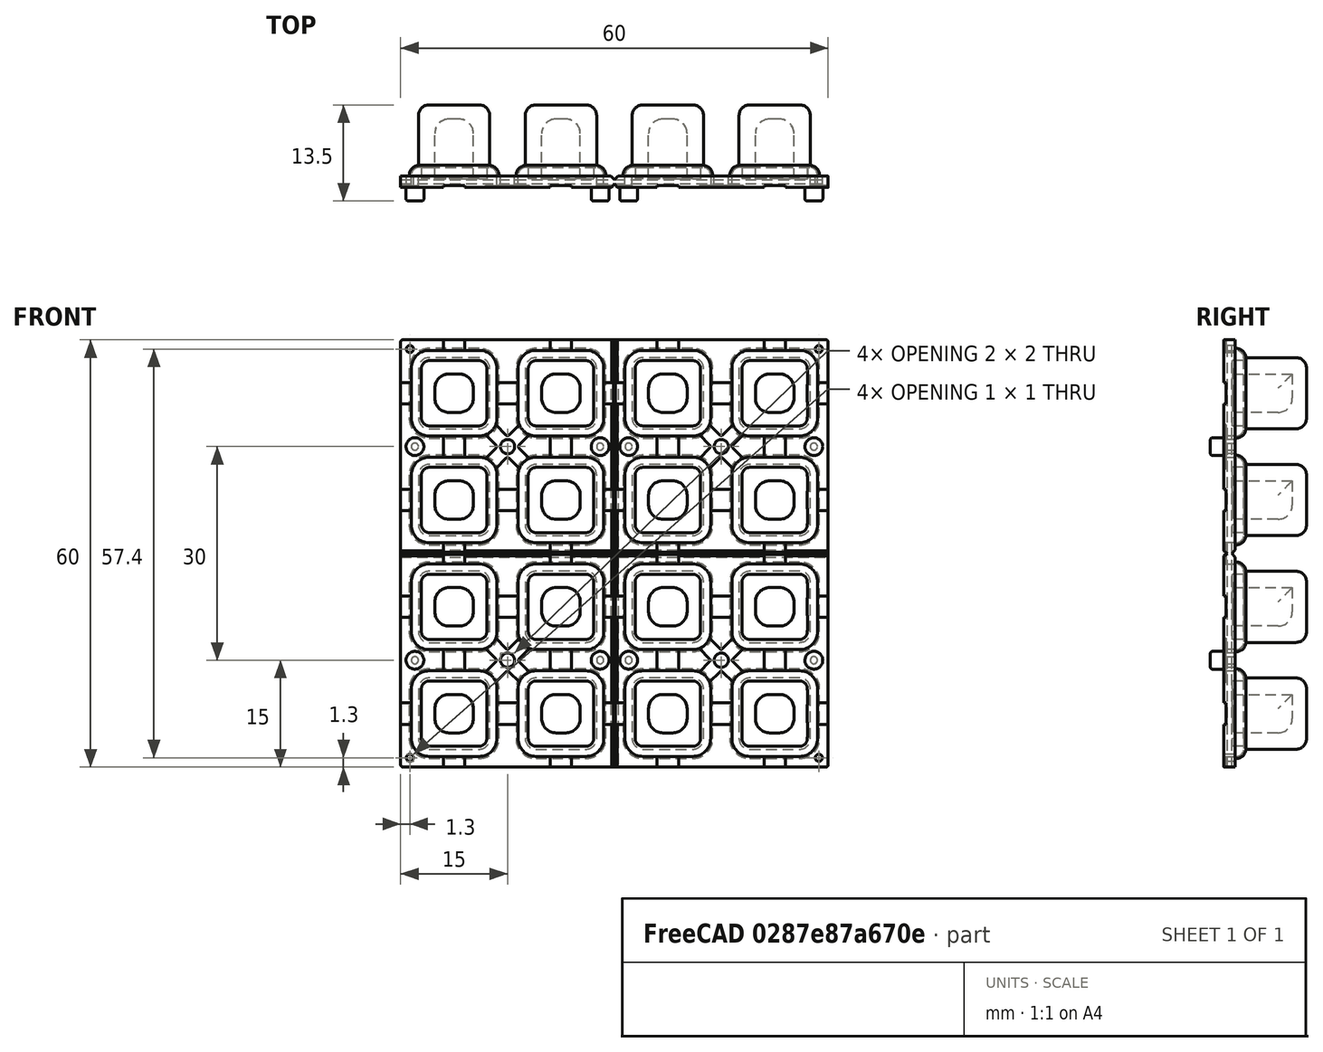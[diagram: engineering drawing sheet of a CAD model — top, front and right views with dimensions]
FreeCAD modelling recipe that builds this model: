
FCSTD DOCUMENT  (FreeCAD 0.20R29177 (Git))
Label: Rubber_pad
License: All rights reserved
LicenseURL: http://en.wikipedia.org/wiki/All_rights_reserved
objects: Part::Feature×1, PartDesign::FeatureBase×1, PartDesign::Body×1, TechDraw::DrawSVGTemplate×1, TechDraw::DrawProjGroupItem×1, TechDraw::DrawProjGroup×1, TechDraw::DrawViewDimension×1, TechDraw::DrawPage×1
note: 3 computed .brp shape members not serialized (recipe doc carries the construction recipe); baked Part::Feature solids carry a one-line shape summary decoded from their .brp

FEATURE [Part::Feature] Part__Feature  label="BUTTON_PAD_REV_1"
  shape: bbox 60 x 13.5 x 60 mm, 1648 faces (baked)
FEATURE [PartDesign::FeatureBase] BaseFeature
  BaseFeature = -> Part__Feature
FEATURE [PartDesign::Body] Body
  BaseFeature = -> Part__Feature
  Group = -> [BaseFeature]
  Origin = -> Origin
  Tip = -> BaseFeature
FEATURE [TechDraw::DrawSVGTemplate] Template
  Height = 297
  Orientation = 1
  Width = 420
FEATURE [TechDraw::DrawProjGroupItem] ProjItem  label="Front"
  CoarseView = false
  Direction = (0,1,0)
  Focus = 100
  HardHidden = false
  IsoCount = 0
  IsoHidden = false
  IsoVisible = false
  LockPosition = true
  Perspective = false
  Rotation = 0
  RotationVector = (0,0,-1)
  ScaleType = 2
  SeamHidden = false
  SeamVisible = true
  SmoothHidden = false
  SmoothVisible = true
  Source = -> [Body]
  Type = 0
  X = 0
  XDirection = (0,0,-1)
  Y = 0
FEATURE [TechDraw::DrawProjGroup] ProjGroup
  Anchor = -> ProjItem
  AutoDistribute = true
  LockPosition = false
  ProjectionType = 0
  Rotation = 0
  ScaleType = 0
  Source = -> [Body]
  Views = -> [ProjItem]
  X = 210
  Y = 148.5
  spacingX = 15
  spacingY = 15
FEATURE [TechDraw::DrawViewDimension] Dimension
  AngleOverride = false
  Arbitrary = false
  ArbitraryTolerances = false
  EqualTolerance = true
  ExtensionAngle = 0
  FormatSpec = %.2f
  FormatSpecOverTolerance = %+.2f
  FormatSpecUnderTolerance = %+.2f
  Inverted = false
  LineAngle = 0
  LockPosition = false
  MeasureType = 1
  OverTolerance = 0
  References2D = -> [ProjItem]
  Rotation = 0
  ScaleType = 0
  TheoreticalExact = false
  Type = 2
  UnderTolerance = 0
  X = -47.2185
  Y = 5.04966
FEATURE [TechDraw::DrawPage] Page
  KeepUpdated = true
  NextBalloonIndex = 1
  ProjectionType = 0
  Template = -> Template
  Views = -> [ProjGroup,Dimension]
